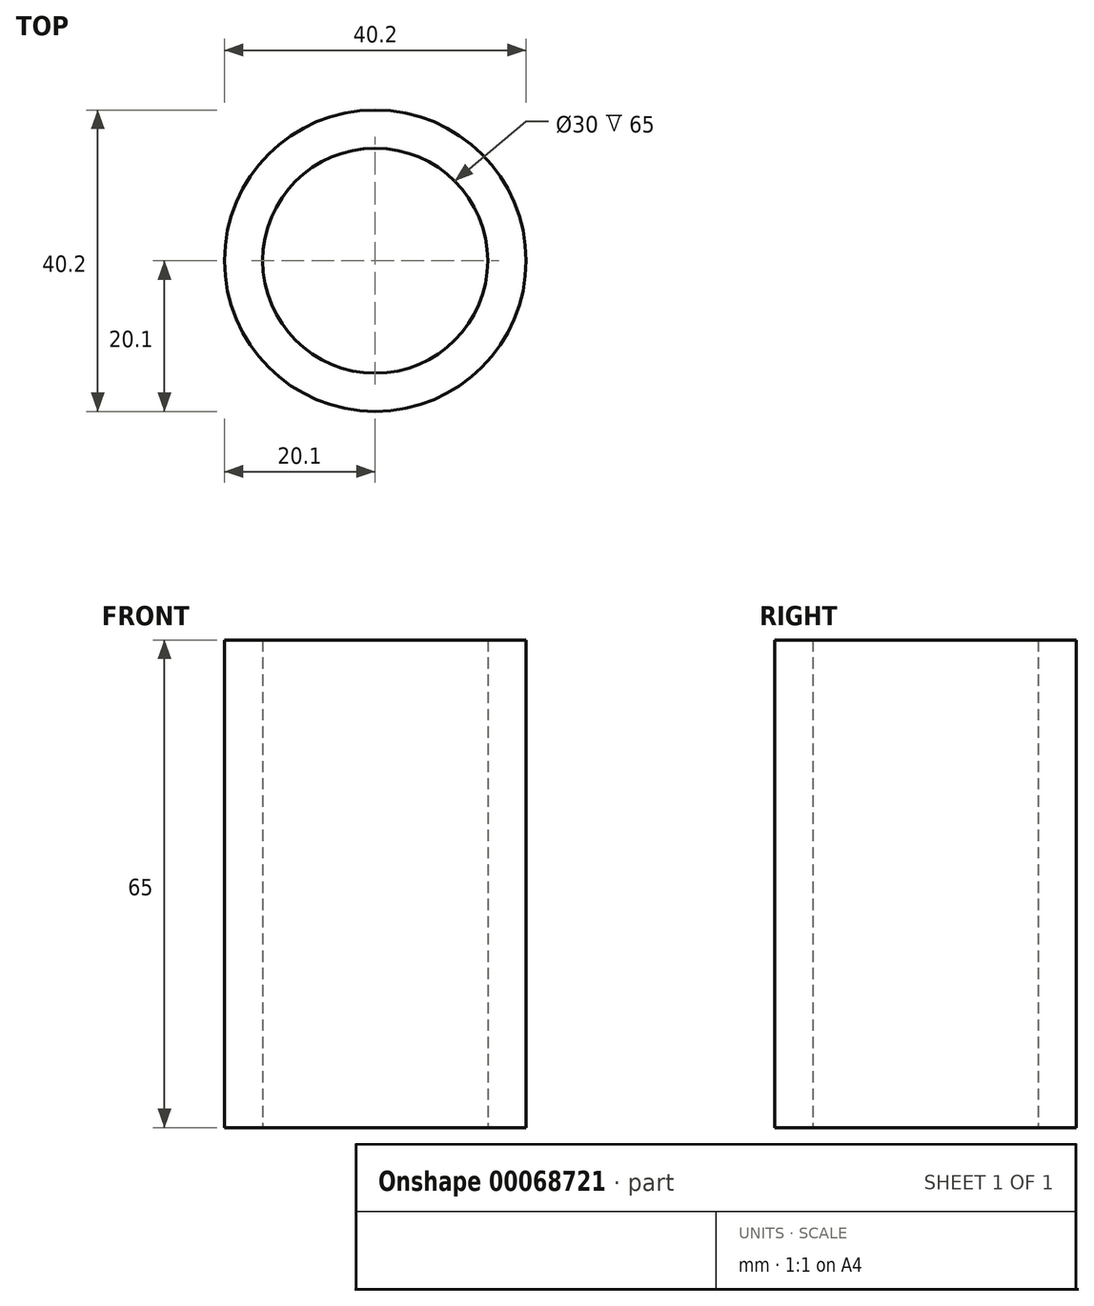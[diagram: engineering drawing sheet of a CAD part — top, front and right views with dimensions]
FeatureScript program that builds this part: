
annotation { "Feature Type Name" : "Feature", "Feature Type Description" : "" }
export const myFeature = defineFeature(function(context is Context, id is Id, definition is map)
    precondition{}
    {
        {
            var Q0;
            Q0=qCreatedBy(makeId("Top.planeOp"),FACE);
            var sketch = newSketch(context, id + "F0", { "sketchPlane" : qUnion([Q0])});
            skCircle(sketch, "E0", {"center": v(0, 0) * mm, "radius": 20.1 * mm});
            skCircle(sketch, "E1", {"center": v(0, 0) * mm, "radius": 15 * mm});
            skSolve(sketch);
        }
        {
            var Q0;
            Q0=makeQuery(id+"F0.imprint","IMPRINT",FACE,{"disambiguationData":[TD([[makeQuery(id+"F0.imprint","IMPRINT",EDGE,{"derivedFrom":sQuery(id+"F0.wireOp",EDGE,"E0")}),1.0]])]});
            extrude(context, id + "F1", {"entities" : qUnion([Q0]), "depth" : 65 * mm});
        }
    });
